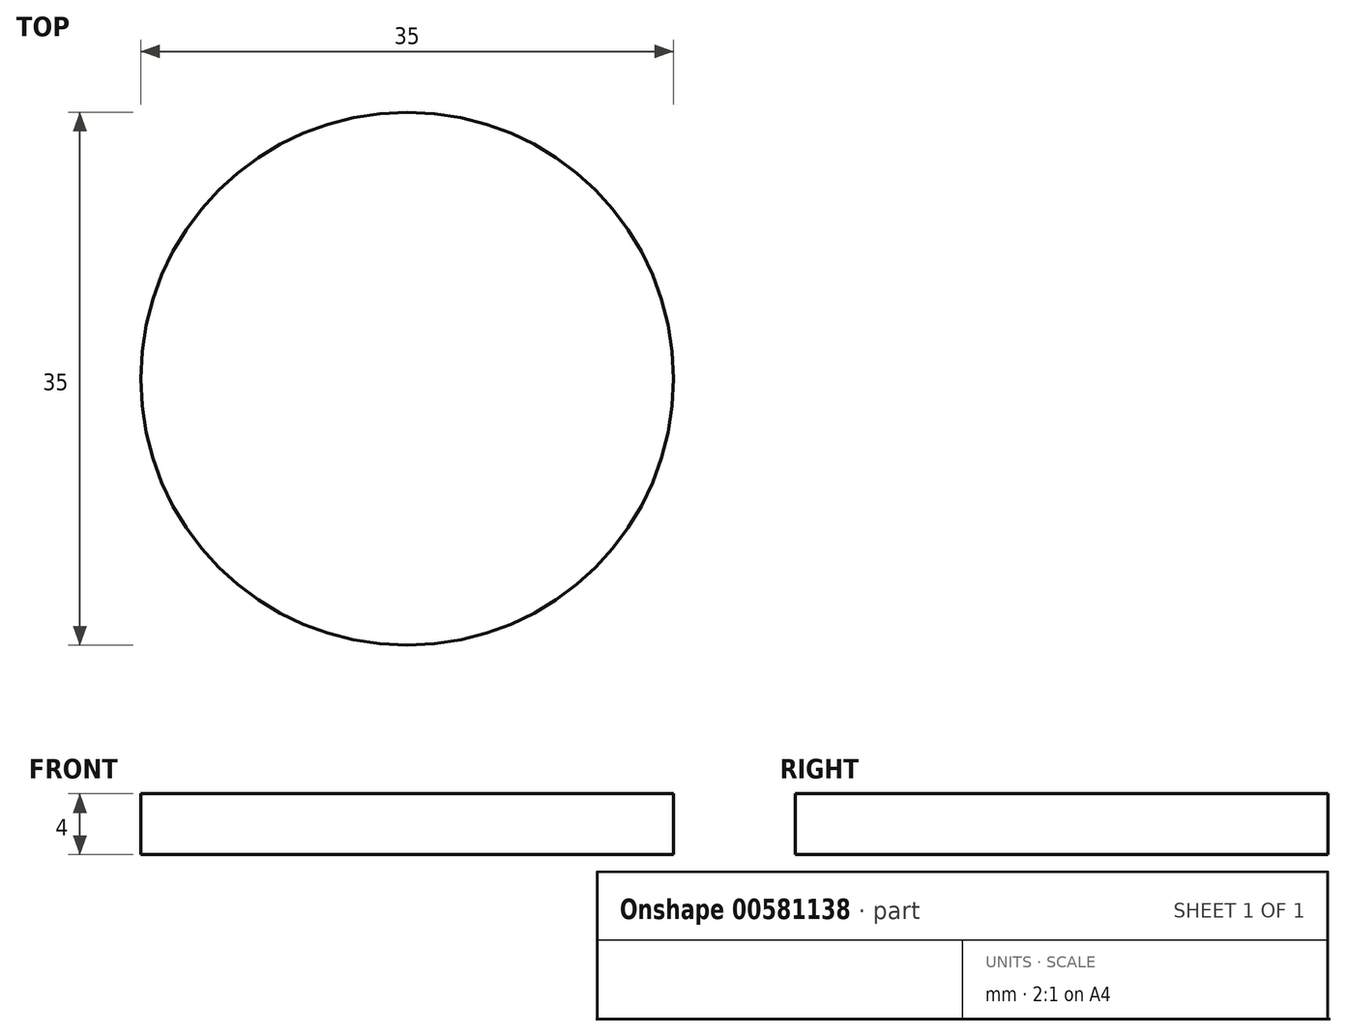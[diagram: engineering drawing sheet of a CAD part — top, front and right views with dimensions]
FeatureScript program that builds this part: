
annotation { "Feature Type Name" : "Feature", "Feature Type Description" : "" }
export const myFeature = defineFeature(function(context is Context, id is Id, definition is map)
    precondition{}
    {
        {
            var Q0;
            Q0=qCreatedBy(makeId("Top.planeOp"),FACE);
            var sketch = newSketch(context, id + "F0", { "sketchPlane" : qUnion([Q0])});
            skCircle(sketch, "E0", {"center": v(0, 0) * mm, "radius": 17.5 * mm});
            skSolve(sketch);
        }
        {
            var Q0;
            Q0 = qSketchRegion(id + "F0", true);
            extrude(context, id + "F1", {"entities" : qUnion([Q0]), "depth" : 4 * mm, "offsetDistance" : 25 * mm});
        }
    });
